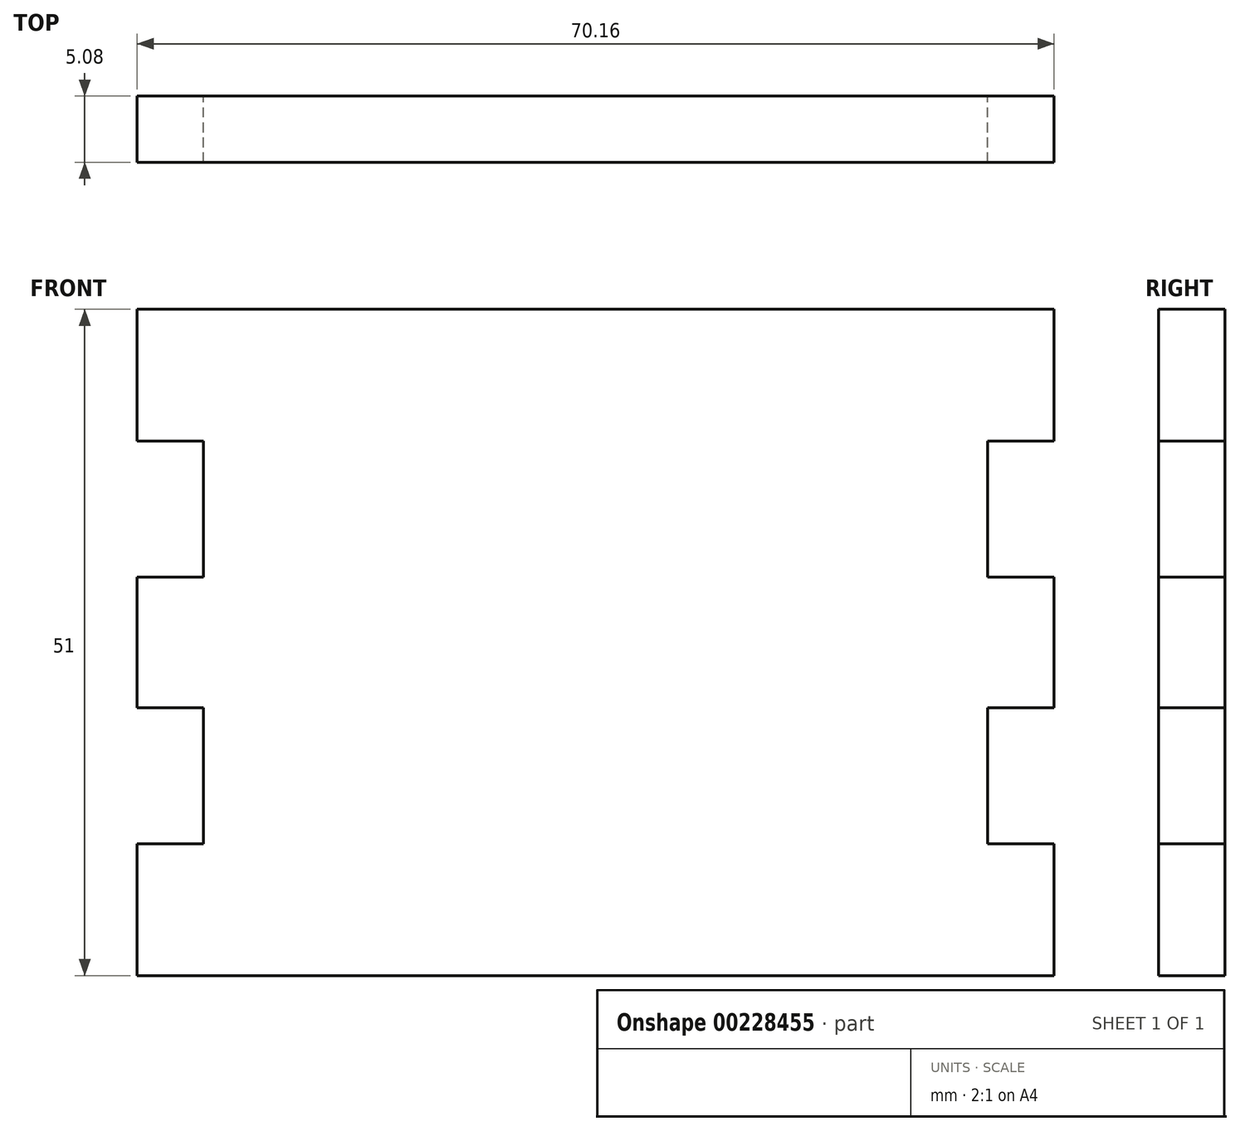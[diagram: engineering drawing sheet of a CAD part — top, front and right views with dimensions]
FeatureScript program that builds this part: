
annotation { "Feature Type Name" : "Feature", "Feature Type Description" : "" }
export const myFeature = defineFeature(function(context is Context, id is Id, definition is map)
    precondition{}
    {
        {
            var Q0;
            Q0=qCreatedBy(makeId("Front.planeOp"),FACE);
            var sketch = newSketch(context, id + "F0", { "sketchPlane" : qUnion([Q0])});
            skLineSegment(sketch, "E0.bottom", {"start": v(0, 0) * mm, "end": v(70.16, 0) * mm});
            skLineSegment(sketch, "E0.top", {"start": v(0, -51) * mm, "end": v(70.16, -51) * mm});
            skLineSegment(sketch, "E0.left", {"start": v(0, 0) * mm, "end": v(0, -51) * mm});
            skLineSegment(sketch, "E0.right", {"start": v(70.16, 0) * mm, "end": v(70.16, -51) * mm});
            skLineSegment(sketch, "E1.bottom", {"start": v(0, -10.1) * mm, "end": v(5.08, -10.1) * mm});
            skLineSegment(sketch, "E1.top", {"start": v(0, -20.5) * mm, "end": v(5.08, -20.5) * mm});
            skLineSegment(sketch, "E1.left", {"start": v(0, -10.1) * mm, "end": v(0, -20.5) * mm});
            skLineSegment(sketch, "E1.right", {"start": v(5.08, -10.1) * mm, "end": v(5.08, -20.5) * mm});
            skLineSegment(sketch, "E2.bottom", {"start": v(0, -30.5) * mm, "end": v(5.08, -30.5) * mm});
            skLineSegment(sketch, "E2.top", {"start": v(0, -40.9) * mm, "end": v(5.08, -40.9) * mm});
            skLineSegment(sketch, "E2.left", {"start": v(0, -30.5) * mm, "end": v(0, -40.9) * mm});
            skLineSegment(sketch, "E2.right", {"start": v(5.08, -30.5) * mm, "end": v(5.08, -40.9) * mm});
            skLineSegment(sketch, "E3", {"start": v(35.08, 52.74) * mm, "end": v(35.08, -68.86) * mm, "construction": true});
            skLineSegment(sketch, "E4.MirrorCS", {"start": v(70.16, -10.1) * mm, "end": v(65.08, -10.1) * mm});
            skLineSegment(sketch, "E5.MirrorCS", {"start": v(65.08, -10.1) * mm, "end": v(65.08, -20.5) * mm});
            skLineSegment(sketch, "E6.MirrorCS", {"start": v(70.16, -20.5) * mm, "end": v(65.08, -20.5) * mm});
            skLineSegment(sketch, "E7.MirrorCS", {"start": v(70.16, -30.5) * mm, "end": v(65.08, -30.5) * mm});
            skLineSegment(sketch, "E8.MirrorCS", {"start": v(65.08, -30.5) * mm, "end": v(65.08, -40.9) * mm});
            skLineSegment(sketch, "E9.MirrorCS", {"start": v(70.16, -40.9) * mm, "end": v(65.08, -40.9) * mm});
            skSolve(sketch);
        }
        {
            var Q0;
            {var subQ5=sQuery(id+"F0.wireOp",EDGE,"E0.bottom");Q0=makeQuery(id+"F0.imprint","IMPRINT",FACE,{"disambiguationData":[TD([[makeQuery(id+"F0.imprint","IMPRINT",EDGE,{"derivedFrom":subQ5}),-1.0]])]});}
            extrude(context, id + "F1", {"entities" : qUnion([Q0]), "depth" : 5.08 * mm});
        }
    });
